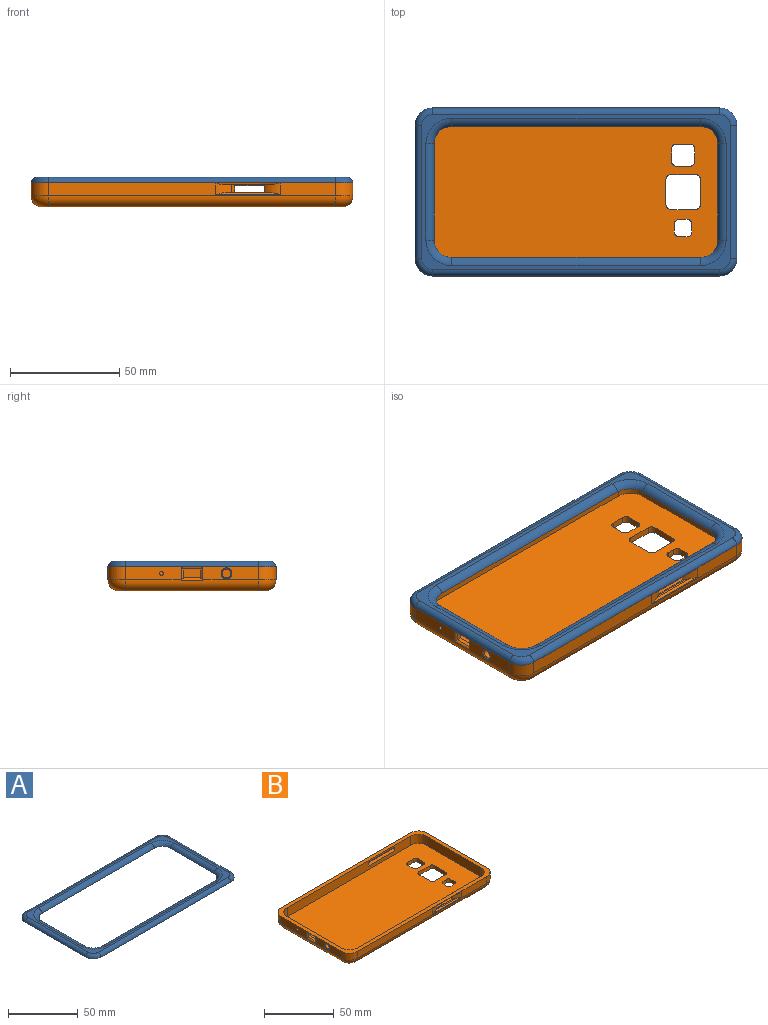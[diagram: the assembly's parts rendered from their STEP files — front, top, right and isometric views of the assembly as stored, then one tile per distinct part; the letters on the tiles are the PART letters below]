
ASSEMBLY  parts=2 mates=1
PART A: 18 faces, bbox 148.9x78.4x4 mm
  f0: plane 147.5x77mm, normal (0,0,-1), area 3557.5mm2, adj f2,f3,f4,f5,f6,f7,f8,f9
  f1: plane 141.55x71.05mm, normal (0,0,1), area 874.6mm2, adj f2,f3,f4,f5,f6,f7,f8,f9
  f2: torus R=5.03mm, axis (0,0,1), area 46.3mm2, adj f0,f1,f3,f4
  f3: cylinder r=3mm len=61mm, axis (0,-1,0), area 263mm2, adj f0,f1,f2,f5
  f4: cylinder r=3mm len=131.5mm, axis (1,0,0), area 566.9mm2, adj f0,f1,f2,f6
  f5: torus R=5.03mm, axis (0,0,1), area 46.3mm2, adj f0,f1,f3,f7
  f6: torus R=5.03mm, axis (0,0,1), area 46.3mm2, adj f0,f1,f4,f8
  f7: cylinder r=3mm len=131.5mm, axis (1,0,0), area 566.9mm2, adj f0,f1,f5,f9
  f8: cylinder r=3mm len=61mm, axis (0,-1,0), area 263mm2, adj f0,f1,f6,f9
  f9: torus R=5.03mm, axis (0,0,1), area 46.3mm2, adj f0,f1,f7,f8
  f10: cylinder r=4mm len=114mm, axis (1,0,0), area 553.2mm2, adj f0,f1,f11,f12
  f11: torus R=11.75mm, axis (0,0,-1), area 73.2mm2, adj f0,f1,f10,f13
  f12: torus R=11.75mm, axis (0,0,-1), area 73.2mm2, adj f0,f1,f10,f14
  f13: cylinder r=4mm len=44mm, axis (0,-1,0), area 213.5mm2, adj f0,f1,f11,f15
  f14: cylinder r=4mm len=44mm, axis (0,-1,0), area 213.5mm2, adj f0,f1,f12,f16
  f15: torus R=11.75mm, axis (0,0,-1), area 73.2mm2, adj f0,f1,f13,f17
  f16: torus R=11.75mm, axis (0,0,-1), area 73.2mm2, adj f0,f1,f14,f17
  f17: cylinder r=4mm len=114mm, axis (1,0,0), area 553.2mm2, adj f0,f1,f15,f16
PART B: 75 faces, bbox 147.5x77x11.1 mm
  f0: plane 25.51x6mm, normal (-1,0,0), area 150.7mm2, adj f7,f13,f26,f69,f74
  f1: plane 25.51x6mm, normal (-1,0,0), area 133.4mm2, adj f7,f18,f26,f70,f71
  f2: plane 55x8mm, normal (1,0,0), area 392.4mm2, adj f6,f7,f12,f17,f64,f65,f66,f67
  f3: plane 131.5x6mm, normal (0,1,0), area 644.8mm2, adj f7,f13,f15,f22,f60,f61,f62,f63
  f4: plane 125.5x8mm, normal (0,-1,0), area 909.5mm2, adj f6,f7,f12,f14,f60,f61,f62,f63
  f5: plane 137.5x67mm, normal (0,0,-1), area 8792.3mm2, adj f20,f21,f22,f23,f24,f25,f26,f27
  f6: plane 141.5x71mm, normal (0,0,1), area 9579.1mm2, adj f2,f4,f10,f11,f12,f14,f16,f17
  f7: plane 147.5x77mm, normal (0,0,1), area 1310.9mm2, adj f0,f1,f2,f3,f4,f8,f9,f10
  f8: plane 131.5x6mm, normal (0,-1,0), area 625.8mm2, adj f7,f18,f19,f25,f57,f58,f59
  f9: plane 61x6mm, normal (1,0,0), area 366mm2, adj f7,f15,f19,f21
  f10: plane 125.5x8mm, normal (0,1,0), area 920.7mm2, adj f6,f7,f16,f17,f54,f58,f59
  f11: plane 55x8mm, normal (-1,0,0), area 440mm2, adj f6,f7,f14,f16
  f12: cylinder r=8mm len=8mm, axis (0,0,1), area 100.5mm2, adj f2,f4,f6,f7
  f13: cylinder r=8mm len=8mm, axis (0,0,-1), area 75.4mm2, adj f0,f3,f7,f24
  f14: cylinder r=8mm len=8mm, axis (0,0,-1), area 100.5mm2, adj f4,f6,f7,f11
  f15: cylinder r=8mm len=8mm, axis (0,0,1), area 75.4mm2, adj f3,f7,f9,f20
  f16: cylinder r=8mm len=8mm, axis (0,0,1), area 100.5mm2, adj f6,f7,f10,f11
  f17: cylinder r=8mm len=8mm, axis (0,0,-1), area 100.5mm2, adj f2,f6,f7,f10
  f18: cylinder r=8mm len=8mm, axis (0,0,1), area 75.4mm2, adj f1,f7,f8,f27
  f19: cylinder r=8mm len=8mm, axis (0,0,-1), area 75.4mm2, adj f7,f8,f9,f23
  f20: torus R=3mm, axis (0,0,1), area 76.3mm2, adj f5,f15,f21,f22
  f21: cylinder r=5mm len=61mm, axis (0,-1,0), area 479.1mm2, adj f5,f9,f20,f23
  f22: cylinder r=5mm len=131.5mm, axis (1,0,0), area 1032.8mm2, adj f3,f5,f20,f24
  f23: torus R=3mm, axis (0,0,1), area 76.3mm2, adj f5,f19,f21,f25
  f24: torus R=3mm, axis (0,0,1), area 76.3mm2, adj f5,f13,f22,f26
  f25: cylinder r=5mm len=131.5mm, axis (-1,0,0), area 1032.8mm2, adj f5,f8,f23,f27
  f26: cylinder r=5mm len=61mm, axis (0,1,0), area 478.7mm2, adj f0,f1,f5,f24,f27,f71,f72,f74
  f27: torus R=3mm, axis (0,0,1), area 76.3mm2, adj f5,f18,f25,f26
  f28: plane 3.6x3mm, normal (1,0,0), area 10.8mm2, adj f5,f6,f40,f43
  f29: plane 3.6x3mm, normal (0,-1,0), area 10.8mm2, adj f5,f6,f42,f43
  f30: plane 3.6x3mm, normal (-1,0,0), area 10.8mm2, adj f5,f6,f41,f42
  f31: plane 3.6x3mm, normal (0,1,0), area 10.8mm2, adj f5,f6,f40,f41
  f32: plane 11.36x3mm, normal (0,1,0), area 34.1mm2, adj f5,f6,f46,f47
  f33: plane 11.65x3mm, normal (1,0,0), area 35mm2, adj f5,f6,f44,f47
  f34: plane 11.36x3mm, normal (0,-1,0), area 34.1mm2, adj f5,f6,f44,f45
  f35: plane 11.65x3mm, normal (-1,0,0), area 35mm2, adj f5,f6,f45,f46
  f36: plane 5.75x3mm, normal (1,0,0), area 17.2mm2, adj f5,f6,f48,f49
  f37: plane 6.23x3mm, normal (0,-1,0), area 18.7mm2, adj f5,f6,f48,f51
  f38: plane 5.75x3mm, normal (-1,0,0), area 17.2mm2, adj f5,f6,f50,f51
  f39: plane 6.23x3mm, normal (0,1,0), area 18.7mm2, adj f5,f6,f49,f50
  f40: cylinder r=2.2mm len=3mm, axis (0,0,-1), area 10.4mm2, adj f5,f6,f28,f31
  f41: cylinder r=2.2mm len=3mm, axis (0,0,1), area 10.4mm2, adj f5,f6,f30,f31
  f42: cylinder r=2.2mm len=3mm, axis (0,0,-1), area 10.4mm2, adj f5,f6,f29,f30
  f43: cylinder r=2.2mm len=3mm, axis (0,0,1), area 10.4mm2, adj f5,f6,f28,f29
  f44: cylinder r=2.2mm len=3mm, axis (0,0,1), area 10.4mm2, adj f5,f6,f33,f34
  f45: cylinder r=2.2mm len=3mm, axis (0,0,-1), area 10.4mm2, adj f5,f6,f34,f35
  f46: cylinder r=2.2mm len=3mm, axis (0,0,1), area 10.4mm2, adj f5,f6,f32,f35
  f47: cylinder r=2.2mm len=3mm, axis (0,0,-1), area 10.4mm2, adj f5,f6,f32,f33
  f48: cylinder r=2.2mm len=3mm, axis (0,0,-1), area 10.4mm2, adj f5,f6,f36,f37
  f49: cylinder r=2.2mm len=3mm, axis (0,0,1), area 10.4mm2, adj f5,f6,f36,f39
  f50: cylinder r=2.2mm len=3mm, axis (0,0,1), area 10.4mm2, adj f5,f6,f38,f39
  f51: cylinder r=2.2mm len=3mm, axis (0,0,-1), area 10.4mm2, adj f5,f6,f37,f38
  f52: plane 20.92x1mm, normal (0,0,1), area 19.1mm2, adj f54,f57,f58,f59
  f53: plane 20.92x1mm, normal (0,0,-1), area 19.1mm2, adj f55,f56,f58,f59
  f54: cylinder r=1mm len=17.56mm, axis (1,0,0), area 25.2mm2, adj f10,f52,f58,f59
  f55: cylinder r=1mm len=17.56mm, axis (-1,0,0), area 24.5mm2, adj f7,f53,f58,f59
  f56: cylinder r=1mm len=29.54mm, axis (1,0,0), area 38.6mm2, adj f7,f53,f58,f59
  f57: cylinder r=1mm len=29.81mm, axis (-1,0,0), area 39.8mm2, adj f8,f52,f58,f59
  f58: cylinder r=10.38mm len=7.3mm, axis (0,0,-1), area 32.7mm2, adj f7,f8,f10,f52,f53,f54,f55,f56
  f59: cylinder r=10.38mm len=7.3mm, axis (0,0,-1), area 32.7mm2, adj f7,f8,f10,f52,f53,f54,f55,f56
  f60: plane 41.2x3mm, normal (0,0,1), area 94.2mm2, adj f3,f4,f62,f63
  f61: plane 41.2x3mm, normal (0,0,-1), area 94.2mm2, adj f3,f4,f62,f63
  f62: cylinder r=9.9mm len=7.1mm, axis (0,0,1), area 27.7mm2, adj f3,f4,f60,f61
  f63: cylinder r=9.9mm len=7.1mm, axis (0,0,1), area 27.7mm2, adj f3,f4,f60,f61
  f64: cylinder r=2mm len=4mm, axis (-1,0,0), area 31.4mm2, adj f2,f70
  f65: plane 4.1x2mm, normal (0,-1,0), area 8.2mm2, adj f2,f66,f68,f74
  f66: plane 7.98x2mm, normal (0,0,1), area 16mm2, adj f2,f65,f67,f72
  f67: plane 4.1x2mm, normal (0,1,0), area 8.2mm2, adj f2,f66,f68,f71
  f68: plane 7.98x2mm, normal (0,0,-1), area 16mm2, adj f2,f65,f67,f73
  f69: cylinder r=0.86mm len=3mm, axis (-1,0,0), area 16.2mm2, adj f0,f2
  f70: torus R=2.5mm, axis (-1,0,0), area 10.8mm2, adj f1,f64
  f71: cylinder r=1mm len=6.04mm, axis (0,0,-1), area 7.6mm2, adj f1,f7,f26,f67,f72,f73
  f72: cylinder r=1mm len=9.95mm, axis (0,1,0), area 13.5mm2, adj f26,f66,f71,f74
  f73: cylinder r=1mm len=9.88mm, axis (0,-1,0), area 13.2mm2, adj f7,f68,f71,f74
  f74: cylinder r=1mm len=6.04mm, axis (0,0,1), area 7.6mm2, adj f0,f7,f26,f65,f72,f73
PLACE A t=(-57.71,-20.5,30.13)mm
PLACE B t=(-58.04,-104.89,62.69)mm fixed
MATE slider A.f0 <-> B.f7  axis (0,0,-1) through (31.23,-59,73.69)mm
